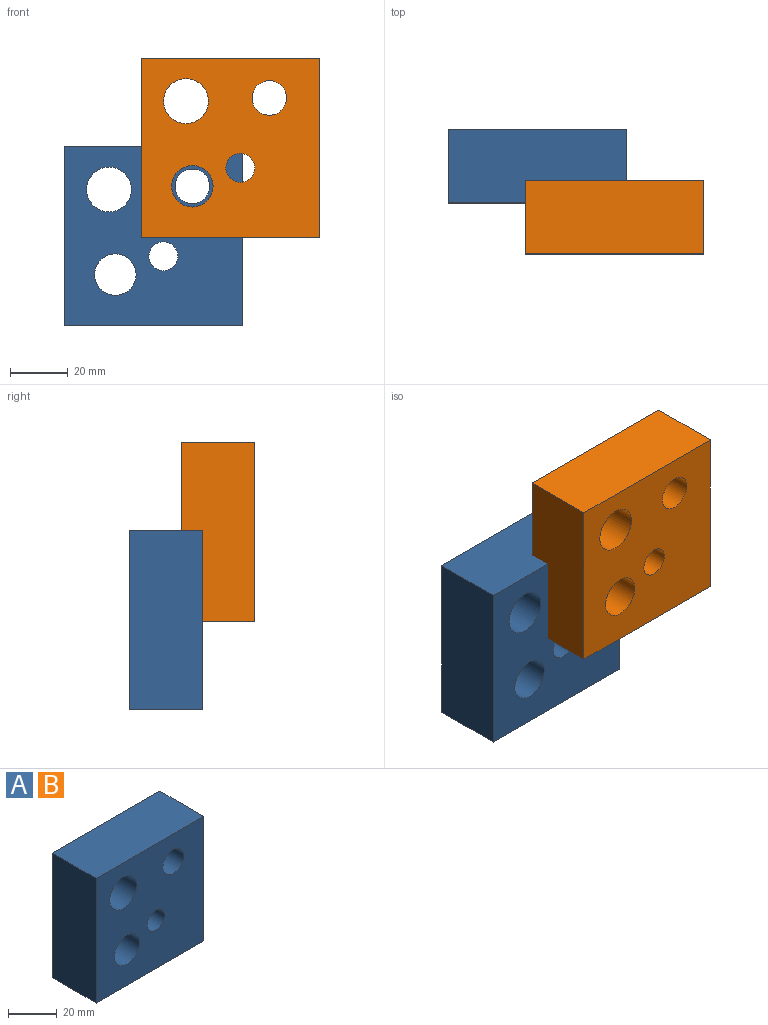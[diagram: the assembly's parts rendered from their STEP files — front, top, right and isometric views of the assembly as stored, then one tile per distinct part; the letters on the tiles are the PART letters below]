
ASSEMBLY  parts=2 mates=1
PART A: 10 faces, bbox 62.1x25.4x62.3 mm
  f0: plane 62.12x25.4mm, normal (0,0,1), area 1577.8mm2, adj f1,f3,f4,f5
  f1: plane 62.32x25.4mm, normal (-1,0,0), area 1582.9mm2, adj f0,f2,f4,f5
  f2: plane 62.12x25.4mm, normal (0,0,-1), area 1577.8mm2, adj f1,f3,f4,f5
  f3: plane 62.32x25.4mm, normal (1,0,0), area 1582.9mm2, adj f0,f2,f4,f5
  f4: plane 62.32x62.12mm, normal (0,-1,0), area 3325.5mm2, adj f0,f1,f2,f3,f6,f7,f8,f9
  f5: plane 62.32x62.12mm, normal (0,1,0), area 3325.5mm2, adj f0,f1,f2,f3,f6,f7,f8,f9
  f6: cylinder r=7.79mm len=25.4mm, axis (0,-1,0), area 1242.5mm2, adj f4,f5
  f7: cylinder r=5.02mm len=25.4mm, axis (0,-1,0), area 801.3mm2, adj f4,f5
  f8: cylinder r=6mm len=25.4mm, axis (0,-1,0), area 958.2mm2, adj f4,f5
  f9: cylinder r=7.2mm len=25.4mm, axis (0,-1,0), area 1148.8mm2, adj f4,f5
PART B: same geometry as A
PLACE A t=(-145.6,-179.51,-143.17)mm
PLACE B rot(axis=(-0.77,-0.02,0.64),0deg) t=(-118.85,-197.29,-112.47)mm
MATE revolute B.f9 <-> A.f8  axis (0,-1,0) through (-232.86,-222.69,-129.06)mm
